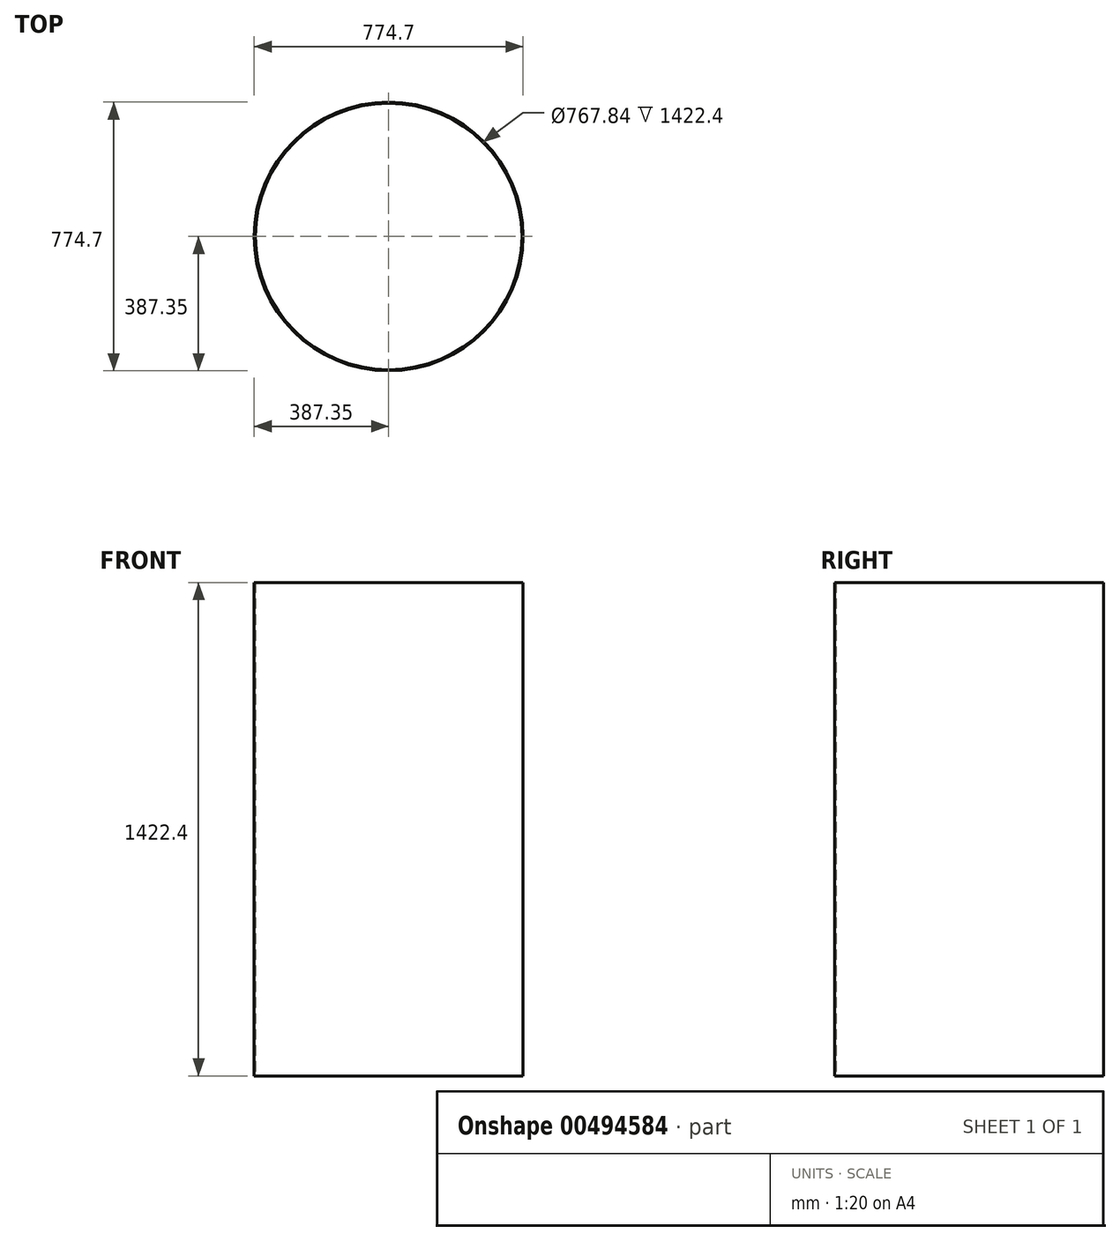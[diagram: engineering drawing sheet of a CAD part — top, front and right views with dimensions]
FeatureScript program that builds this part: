
annotation { "Feature Type Name" : "Feature", "Feature Type Description" : "" }
export const myFeature = defineFeature(function(context is Context, id is Id, definition is map)
    precondition{}
    {
        {
            var Q0;
            Q0=qCreatedBy(makeId("Top.planeOp"),FACE);
            var sketch = newSketch(context, id + "F0", { "sketchPlane" : qUnion([Q0])});
            skCircle(sketch, "E0", {"center": v(0, 0) * mm, "radius": 387.35 * mm});
            skCircle(sketch, "E1", {"center": v(0, 0) * mm, "radius": 383.92 * mm});
            skSolve(sketch);
        }
        {
            var Q0;
            Q0 = qSketchRegion(id + "F0", true);
            extrude(context, id + "F1", {"entities" : qUnion([Q0]), "depth" : 1422.4 * mm});
        }
    });
